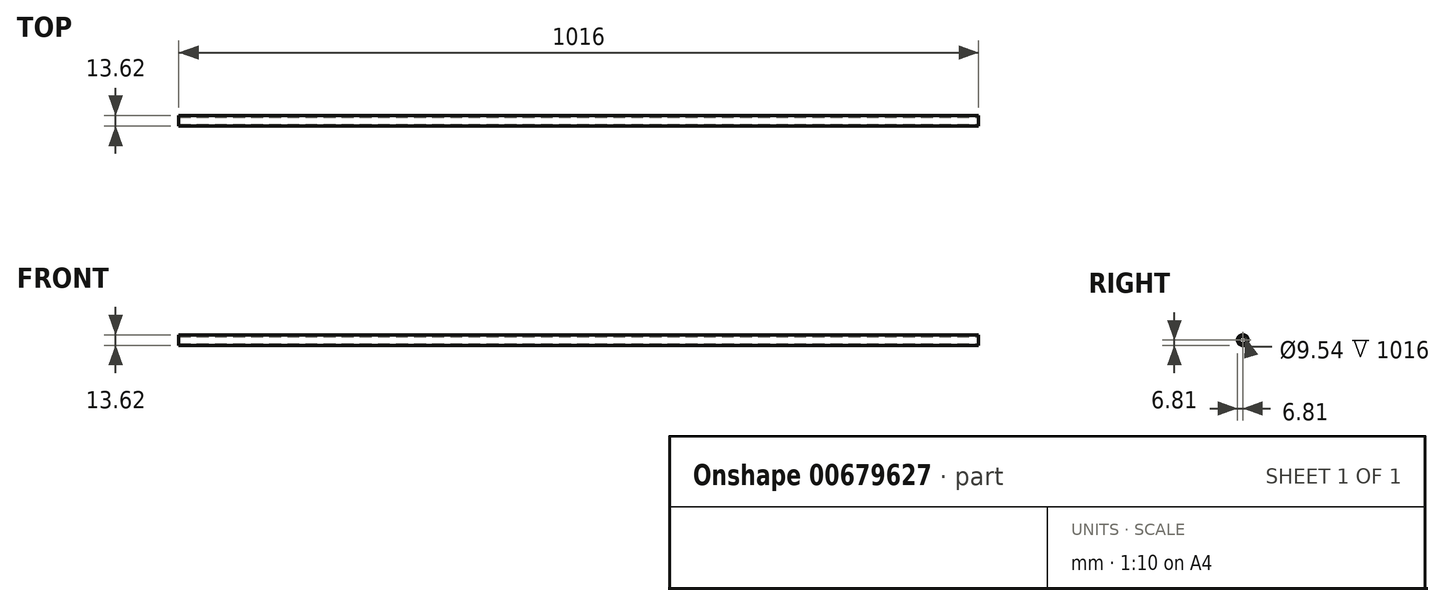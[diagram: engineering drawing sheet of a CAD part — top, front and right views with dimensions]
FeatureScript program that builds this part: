
annotation { "Feature Type Name" : "Feature", "Feature Type Description" : "" }
export const myFeature = defineFeature(function(context is Context, id is Id, definition is map)
    precondition{}
    {
        {
            var Q0;
            Q0=qCreatedBy(makeId("Right.planeOp"),FACE);
            var sketch = newSketch(context, id + "F0", { "sketchPlane" : qUnion([Q0])});
            skCircle(sketch, "E0", {"center": v(0, 0) * mm, "radius": 6.81 * mm});
            skSolve(sketch);
        }
        {
            var Q0;
            Q0=makeQuery(id+"F0.imprint","IMPRINT",FACE,{"disambiguationData":[TD([[makeQuery(id+"F0.imprint","IMPRINT",EDGE,{"derivedFrom":sQuery(id+"F0.wireOp",EDGE,"E0")}),1.0]])]});
            extrude(context, id + "F1", {"entities" : qUnion([Q0]), "oppositeDirection" : true, "depth" : 1016 * mm, "offsetDistance" : 25.4 * mm});
        }
        {
            var Q0;
            Q0=makeQuery(id+"F1.opExtrude","CAP_FACE",FACE,{"disambiguationData":[OSD([sQuery(id+"F0.wireOp",EDGE,"E0")])],"isStart":true});
            var sketch = newSketch(context, id + "F2", { "sketchPlane" : qUnion([Q0])});
            skCircle(sketch, "E1", {"center": v(0, 0) * mm, "radius": 4.77 * mm});
            skSolve(sketch);
        }
        {
            var Q0;
            Q0=makeQuery(id+"F2.imprint","IMPRINT",FACE,{"disambiguationData":[TD([[makeQuery(id+"F2.imprint","IMPRINT",EDGE,{"derivedFrom":sQuery(id+"F2.wireOp",EDGE,"E1")}),1.0]])]});
            extrude(context, id + "F3", {"entities" : qUnion([Q0]), "operationType" : NewBodyOperationType.REMOVE, "endBound" : BoundingType.THROUGH_ALL, "oppositeDirection" : true, "depth" : 25.4 * mm, "offsetDistance" : 25.4 * mm});
        }
    });
